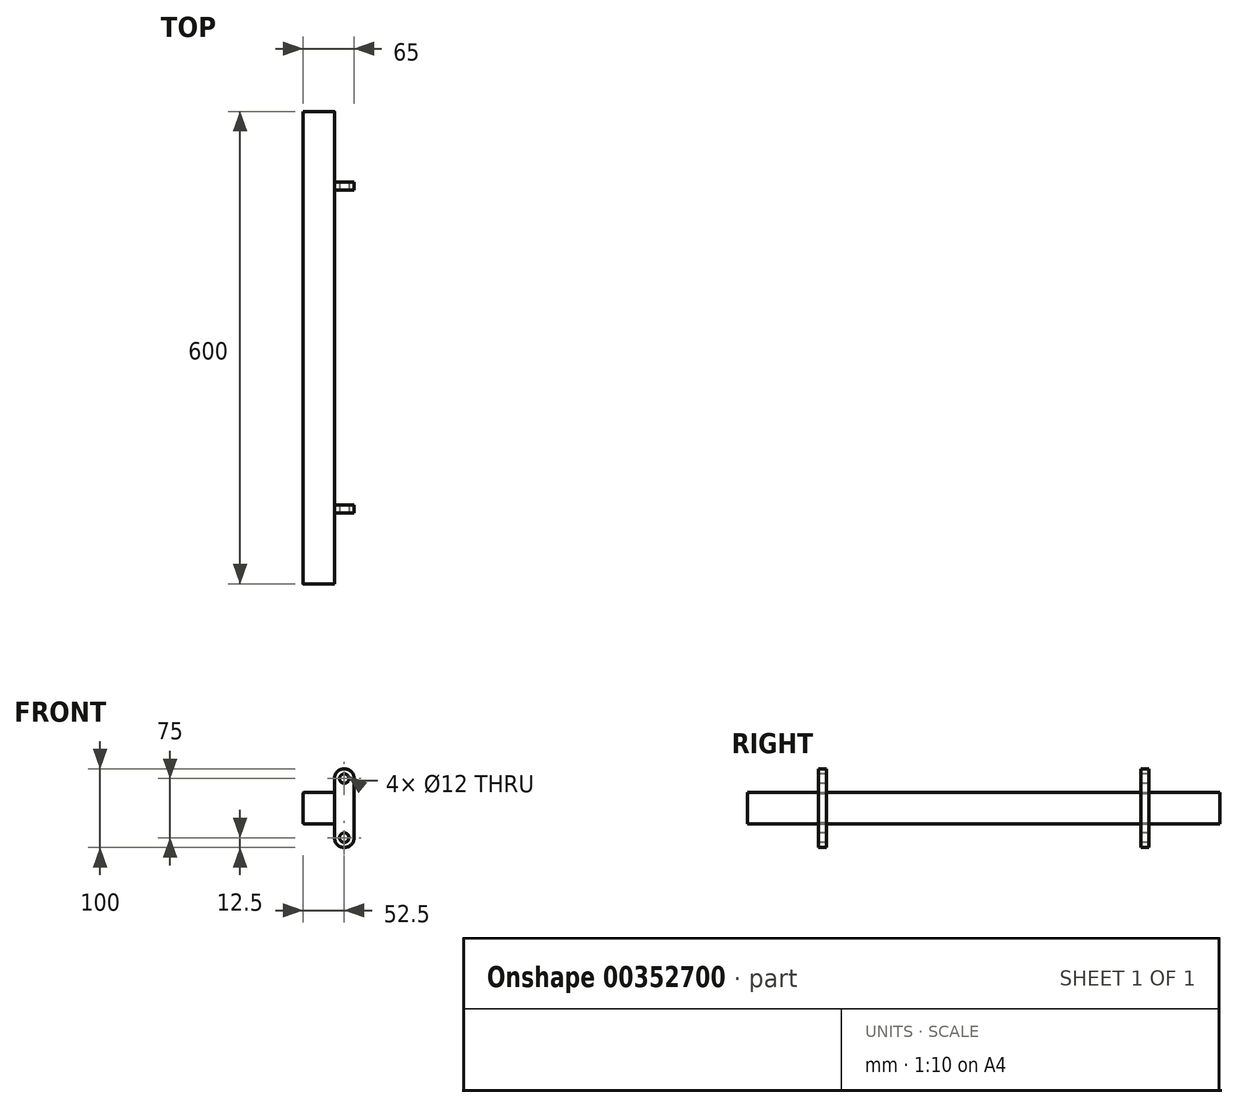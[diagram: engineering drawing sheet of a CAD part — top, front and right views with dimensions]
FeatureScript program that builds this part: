
annotation { "Feature Type Name" : "Feature", "Feature Type Description" : "" }
export const myFeature = defineFeature(function(context is Context, id is Id, definition is map)
    precondition{}
    {
        {
            var Q0;
            Q0=qCreatedBy(makeId("Front.planeOp"),FACE);
            var sketch = newSketch(context, id + "F0", { "sketchPlane" : qUnion([Q0])});
            skLineSegment(sketch, "E0.bottom", {"start": v(20, -20) * mm, "end": v(-20, -20) * mm});
            skLineSegment(sketch, "E0.top", {"start": v(20, 20) * mm, "end": v(-20, 20) * mm});
            skLineSegment(sketch, "E0.left", {"start": v(20, -20) * mm, "end": v(20, 20) * mm});
            skLineSegment(sketch, "E0.right", {"start": v(-20, -20) * mm, "end": v(-20, 20) * mm});
            skPoint(sketch, "E0.middle", {"position": v(0, 0) * mm});
            skSolve(sketch);
        }
        {
            var Q0;
            Q0=makeQuery(id+"F0.imprint","IMPRINT",FACE,{"disambiguationData":[TD([[makeQuery(id+"F0.imprint","IMPRINT",EDGE,{"derivedFrom":sQuery(id+"F0.wireOp",EDGE,"E0.bottom")}),-1.0]])]});
            extrude(context, id + "F1", {"entities" : qUnion([Q0]), "depth" : 600 * mm});
        }
        {
            var Q0;
            Q0=makeQuery(id+"F1.opExtrude","SWEPT_EDGE",EDGE,{"disambiguationData":[OSD([sQuery(id+"F0.wireOp",EDGE,"E0.top"),sQuery(id+"F0.wireOp",EDGE,"E0.right")])]});
            var Q1;
            Q1=makeQuery(id+"F1.opExtrude","SWEPT_EDGE",EDGE,{"disambiguationData":[OSD([sQuery(id+"F0.wireOp",EDGE,"E0.bottom"),sQuery(id+"F0.wireOp",EDGE,"E0.right")])]});
            var Q2;
            Q2=makeQuery(id+"F1.opExtrude","SWEPT_EDGE",EDGE,{"disambiguationData":[OSD([sQuery(id+"F0.wireOp",EDGE,"E0.top"),sQuery(id+"F0.wireOp",EDGE,"E0.left")])]});
            var Q3;
            Q3=makeQuery(id+"F1.opExtrude","SWEPT_EDGE",EDGE,{"disambiguationData":[OSD([sQuery(id+"F0.wireOp",EDGE,"E0.bottom"),sQuery(id+"F0.wireOp",EDGE,"E0.left")])]});
            fillet(context, id + "F2", {"entities" : qUnion([Q0, Q1, Q2, Q3]), "radius" : 1.5 * mm, "tangentPropagation" : true, "allowEdgeOverflow" : false});
        }
        {
            var Q0;
            Q0=makeQuery(id+"F1.opExtrude","SWEPT_FACE",FACE,{"disambiguationData":[OSD([sQuery(id+"F0.wireOp",EDGE,"E0.left")])]});
            var sketch = newSketch(context, id + "F3", { "sketchPlane" : qUnion([Q0])});
            skLineSegment(sketch, "E1.bottom", {"start": v(-500, -50) * mm, "end": v(-510, -50) * mm});
            skLineSegment(sketch, "E1.top", {"start": v(-500, 50) * mm, "end": v(-510, 50) * mm});
            skLineSegment(sketch, "E1.left", {"start": v(-500, -50) * mm, "end": v(-500, 50) * mm});
            skLineSegment(sketch, "E1.right", {"start": v(-510, -50) * mm, "end": v(-510, 50) * mm});
            skPoint(sketch, "E1.middle", {"position": v(-505, 0) * mm});
            skLineSegment(sketch, "E2.bottom", {"start": v(-90, -50) * mm, "end": v(-100, -50) * mm});
            skLineSegment(sketch, "E2.top", {"start": v(-90, 50) * mm, "end": v(-100, 50) * mm});
            skLineSegment(sketch, "E2.left", {"start": v(-90, -50) * mm, "end": v(-90, 50) * mm});
            skLineSegment(sketch, "E2.right", {"start": v(-100, -50) * mm, "end": v(-100, 50) * mm});
            skPoint(sketch, "E2.middle", {"position": v(-95, 0) * mm});
            skSolve(sketch);
        }
        {
            var Q0;
            Q0 = qSketchRegion(id + "F3", true);
            extrude(context, id + "F4", {"entities" : qUnion([Q0]), "operationType" : NewBodyOperationType.ADD, "depth" : 25 * mm});
        }
        {
            var Q0;
            Q0=makeQuery(id+"F4.opExtrude","CAP_EDGE",EDGE,{"disambiguationData":[OSD([sQuery(id+"F3.wireOp",EDGE,"E1.top")])],"isStart":false});
            var Q1;
            Q1=makeQuery(id+"F4.opExtrude","CAP_EDGE",EDGE,{"disambiguationData":[OSD([sQuery(id+"F3.wireOp",EDGE,"E1.top")])],"isStart":true});
            var Q2;
            Q2=makeQuery(id+"F4.opExtrude","CAP_EDGE",EDGE,{"disambiguationData":[OSD([sQuery(id+"F3.wireOp",EDGE,"E2.top")])],"isStart":false});
            var Q3;
            Q3=makeQuery(id+"F4.opExtrude","CAP_EDGE",EDGE,{"disambiguationData":[OSD([sQuery(id+"F3.wireOp",EDGE,"E2.top")])],"isStart":true});
            var Q4;
            Q4=makeQuery(id+"F4.opExtrude","CAP_EDGE",EDGE,{"disambiguationData":[OSD([sQuery(id+"F3.wireOp",EDGE,"E2.bottom")])],"isStart":false});
            var Q5;
            Q5=makeQuery(id+"F4.opExtrude","CAP_EDGE",EDGE,{"disambiguationData":[OSD([sQuery(id+"F3.wireOp",EDGE,"E1.bottom")])],"isStart":false});
            var Q6;
            Q6=makeQuery(id+"F4.opExtrude","CAP_EDGE",EDGE,{"disambiguationData":[OSD([sQuery(id+"F3.wireOp",EDGE,"E1.bottom")])],"isStart":true});
            var Q7;
            Q7=makeQuery(id+"F4.opExtrude","CAP_EDGE",EDGE,{"disambiguationData":[OSD([sQuery(id+"F3.wireOp",EDGE,"E2.bottom")])],"isStart":true});
            fillet(context, id + "F5", {"entities" : qUnion([Q0, Q1, Q2, Q3, Q4, Q5, Q6, Q7]), "radius" : 12.5 * mm, "tangentPropagation" : true, "allowEdgeOverflow" : false});
        }
        {
            var Q0;
            Q0=makeQuery(id+"F4.opExtrude","SWEPT_FACE",FACE,{"disambiguationData":[OSD([sQuery(id+"F3.wireOp",EDGE,"E1.right")])]});
            var sketch = newSketch(context, id + "F6", { "sketchPlane" : qUnion([Q0])});
            skLineSegment(sketch, "E3", {"start": v(32.5, 39.93) * mm, "end": v(32.5, -43.3) * mm});
            skPoint(sketch, "E3.startSnap0", {"position": v(32.5, 50) * mm});
            skLineSegment(sketch, "E4", {"start": v(20, -37.5) * mm, "end": v(45, -37.5) * mm});
            skLineSegment(sketch, "E5", {"start": v(20, 37.5) * mm, "end": v(45, 37.5) * mm});
            skPoint(sketch, "E6", {"position": v(32.5, 37.5) * mm});
            skPoint(sketch, "E7", {"position": v(32.5, -37.5) * mm});
            skSolve(sketch);
        }
        {
            var Q0;
            Q0=sQuery(id+"F6.wireOp",VERTEX,"E6");
            var Q1;
            Q1=sQuery(id+"F6.wireOp",VERTEX,"E7");
            var Q2;
            Q2=makeQuery(id+"F1.opExtrude","SWEPT_BODY",BODY,{"disambiguationData":[OSD([sQuery(id+"F0.wireOp",EDGE,"E0.bottom"),sQuery(id+"F0.wireOp",EDGE,"E0.top"),sQuery(id+"F0.wireOp",EDGE,"E0.left"),sQuery(id+"F0.wireOp",EDGE,"E0.right")])]});
            hole(context, id + "F7", {"style" : HoleStyle.SIMPLE, "endStyle" : HoleEndStyle.BLIND, "holeDiameter" : 12 * mm, "holeDepth" : 450 * mm, "isTappedThrough" : true, "tappedDepth" : 12 * mm, "tapClearance" : 3, "locations" : qUnion([Q0, Q1]), "scope" : qUnion([Q2])});
        }
    });
